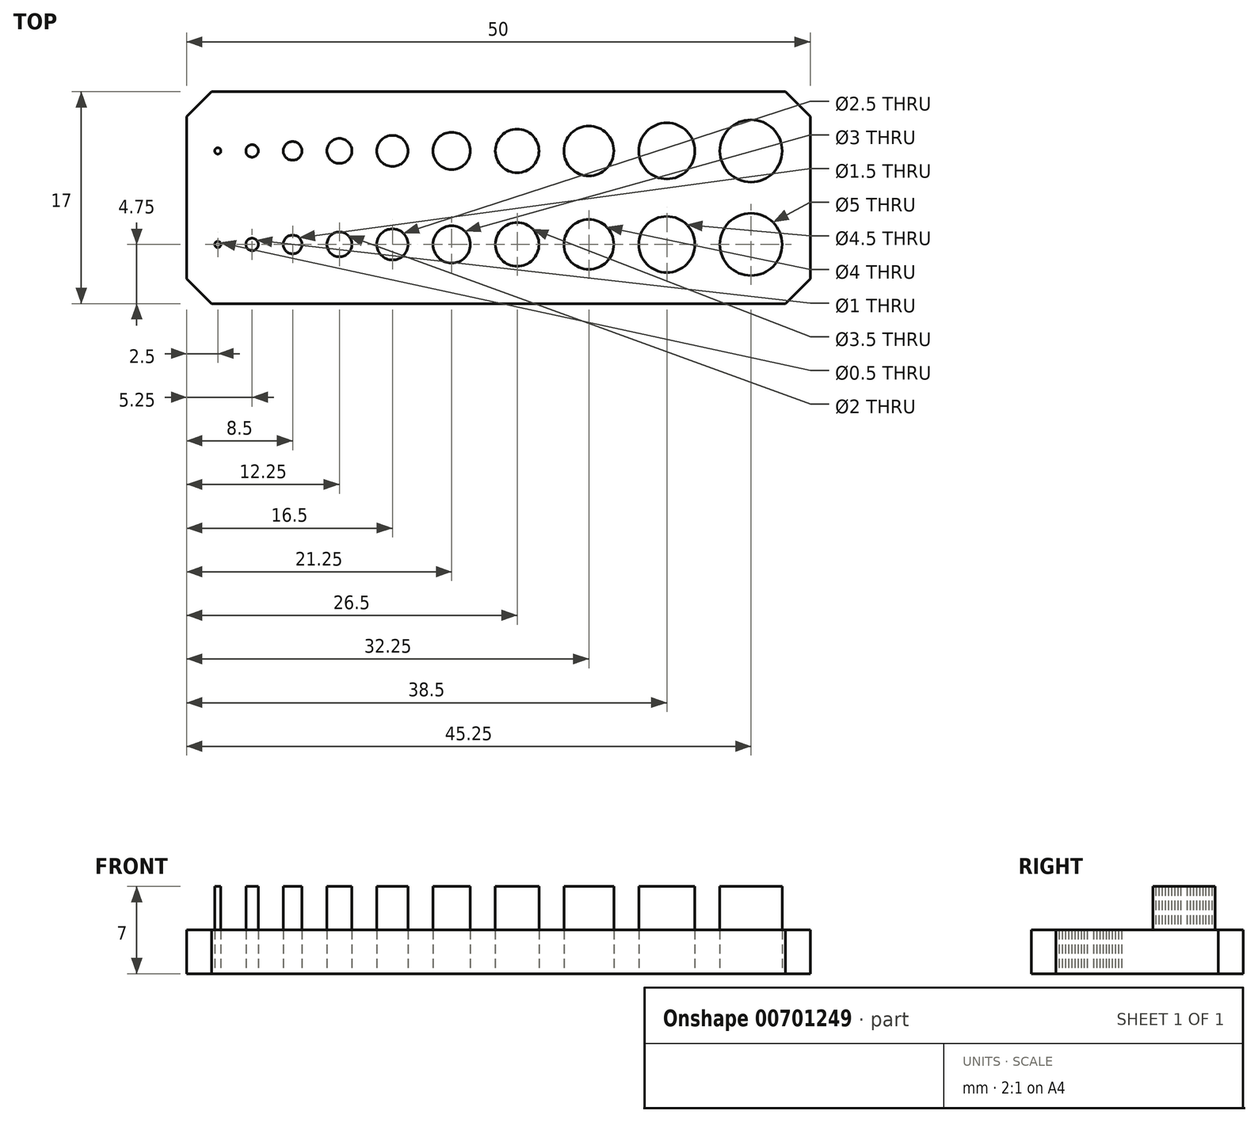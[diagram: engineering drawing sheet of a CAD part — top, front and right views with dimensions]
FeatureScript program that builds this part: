
annotation { "Feature Type Name" : "Feature", "Feature Type Description" : "" }
export const myFeature = defineFeature(function(context is Context, id is Id, definition is map)
    precondition{}
    {
        {
            var Q0;
            Q0=qCreatedBy(makeId("Top.planeOp"),FACE);
            var sketch = newSketch(context, id + "F0", { "sketchPlane" : qUnion([Q0])});
            skLineSegment(sketch, "E0.bottom", {"start": v(25, 8.5) * mm, "end": v(-25, 8.5) * mm});
            skLineSegment(sketch, "E0.top", {"start": v(25, -8.5) * mm, "end": v(-25, -8.5) * mm});
            skLineSegment(sketch, "E0.left", {"start": v(25, 8.5) * mm, "end": v(25, -8.5) * mm});
            skLineSegment(sketch, "E0.right", {"start": v(-25, 8.5) * mm, "end": v(-25, -8.5) * mm});
            skPoint(sketch, "E0.middle", {"position": v(0, 0) * mm});
            skCircle(sketch, "E1", {"center": v(-22.5, 3.75) * mm, "radius": 0.25 * mm});
            skCircle(sketch, "E2", {"center": v(-19.75, 3.75) * mm, "radius": 0.5 * mm});
            skLineSegment(sketch, "E3", {"start": v(-22.25, 3.75) * mm, "end": v(-20.25, 3.75) * mm, "construction": true});
            skLineSegment(sketch, "E4", {"start": v(-19.25, 3.75) * mm, "end": v(-17.25, 3.75) * mm, "construction": true});
            skCircle(sketch, "E5", {"center": v(-16.5, 3.75) * mm, "radius": 0.75 * mm});
            skLineSegment(sketch, "E6", {"start": v(-15.75, 3.75) * mm, "end": v(-13.75, 3.75) * mm, "construction": true});
            skCircle(sketch, "E7", {"center": v(-12.75, 3.75) * mm, "radius": 1 * mm});
            skLineSegment(sketch, "E8", {"start": v(-11.75, 3.75) * mm, "end": v(-9.75, 3.75) * mm, "construction": true});
            skCircle(sketch, "E9", {"center": v(-8.5, 3.75) * mm, "radius": 1.25 * mm});
            skLineSegment(sketch, "E10", {"start": v(-7.25, 3.75) * mm, "end": v(-5.25, 3.75) * mm, "construction": true});
            skCircle(sketch, "E11", {"center": v(-3.75, 3.75) * mm, "radius": 1.5 * mm});
            skLineSegment(sketch, "E12", {"start": v(-2.25, 3.75) * mm, "end": v(-0.25, 3.75) * mm, "construction": true});
            skCircle(sketch, "E13", {"center": v(1.5, 3.75) * mm, "radius": 1.75 * mm});
            skLineSegment(sketch, "E14", {"start": v(3.25, 3.75) * mm, "end": v(5.25, 3.75) * mm, "construction": true});
            skCircle(sketch, "E15", {"center": v(7.25, 3.75) * mm, "radius": 2 * mm});
            skLineSegment(sketch, "E16", {"start": v(9.25, 3.75) * mm, "end": v(11.25, 3.75) * mm, "construction": true});
            skCircle(sketch, "E17", {"center": v(13.5, 3.75) * mm, "radius": 2.25 * mm});
            skLineSegment(sketch, "E18", {"start": v(15.75, 3.75) * mm, "end": v(17.75, 3.75) * mm, "construction": true});
            skCircle(sketch, "E19", {"center": v(20.25, 3.75) * mm, "radius": 2.5 * mm});
            skLineSegment(sketch, "E20", {"start": v(22.75, 3.75) * mm, "end": v(25, 3.75) * mm, "construction": true});
            skLineSegment(sketch, "E21", {"start": v(-22.75, 3.75) * mm, "end": v(-25, 3.75) * mm, "construction": true});
            skLineSegment(sketch, "E22", {"start": v(0, 0) * mm, "end": v(7.3, 0) * mm, "construction": true});
            skCircle(sketch, "E23.MirrorC", {"center": v(-22.5, -3.75) * mm, "radius": 0.25 * mm});
            skCircle(sketch, "E24.MirrorC", {"center": v(1.5, -3.75) * mm, "radius": 1.75 * mm});
            skCircle(sketch, "E25.MirrorC", {"center": v(-19.75, -3.75) * mm, "radius": 0.5 * mm});
            skCircle(sketch, "E26.MirrorC", {"center": v(7.25, -3.75) * mm, "radius": 2 * mm});
            skCircle(sketch, "E27.MirrorC", {"center": v(13.5, -3.75) * mm, "radius": 2.25 * mm});
            skCircle(sketch, "E28.MirrorC", {"center": v(20.25, -3.75) * mm, "radius": 2.5 * mm});
            skCircle(sketch, "E29.MirrorC", {"center": v(-16.5, -3.75) * mm, "radius": 0.75 * mm});
            skCircle(sketch, "E30.MirrorC", {"center": v(-3.75, -3.75) * mm, "radius": 1.5 * mm});
            skCircle(sketch, "E31.MirrorC", {"center": v(-8.5, -3.75) * mm, "radius": 1.25 * mm});
            skCircle(sketch, "E32.MirrorC", {"center": v(-12.75, -3.75) * mm, "radius": 1 * mm});
            skLineSegment(sketch, "E33", {"start": v(20.25, 6.25) * mm, "end": v(20.25, 8.5) * mm, "construction": true});
            skSolve(sketch);
        }
        {
            var Q0;
            Q0=qSketchRegion(id+"F0",true);
            extrude(context, id + "F1", {"entities" : qUnion([Q0]), "depth" : 3.5 * mm, "offsetDistance" : 25 * mm});
        }
        {
            var Q0;
            Q0=makeQuery(id+"F0.imprint","IMPRINT",FACE,{"disambiguationData":[TD([[makeQuery(id+"F0.imprint","IMPRINT",EDGE,{"derivedFrom":sQuery(id+"F0.wireOp",EDGE,"E1")}),1.0]])]});
            var Q1;
            Q1=makeQuery(id+"F0.imprint","IMPRINT",FACE,{"disambiguationData":[TD([[makeQuery(id+"F0.imprint","IMPRINT",EDGE,{"derivedFrom":sQuery(id+"F0.wireOp",EDGE,"E2")}),1.0]])]});
            var Q2;
            Q2=makeQuery(id+"F0.imprint","IMPRINT",FACE,{"disambiguationData":[TD([[makeQuery(id+"F0.imprint","IMPRINT",EDGE,{"derivedFrom":sQuery(id+"F0.wireOp",EDGE,"E5")}),1.0]])]});
            var Q3;
            Q3=makeQuery(id+"F0.imprint","IMPRINT",FACE,{"disambiguationData":[TD([[makeQuery(id+"F0.imprint","IMPRINT",EDGE,{"derivedFrom":sQuery(id+"F0.wireOp",EDGE,"E7")}),1.0]])]});
            var Q4;
            Q4=makeQuery(id+"F0.imprint","IMPRINT",FACE,{"disambiguationData":[TD([[makeQuery(id+"F0.imprint","IMPRINT",EDGE,{"derivedFrom":sQuery(id+"F0.wireOp",EDGE,"E9")}),1.0]])]});
            var Q5;
            Q5=makeQuery(id+"F0.imprint","IMPRINT",FACE,{"disambiguationData":[TD([[makeQuery(id+"F0.imprint","IMPRINT",EDGE,{"derivedFrom":sQuery(id+"F0.wireOp",EDGE,"E11")}),1.0]])]});
            var Q6;
            Q6=makeQuery(id+"F0.imprint","IMPRINT",FACE,{"disambiguationData":[TD([[makeQuery(id+"F0.imprint","IMPRINT",EDGE,{"derivedFrom":sQuery(id+"F0.wireOp",EDGE,"E13")}),1.0]])]});
            var Q7;
            Q7=makeQuery(id+"F0.imprint","IMPRINT",FACE,{"disambiguationData":[TD([[makeQuery(id+"F0.imprint","IMPRINT",EDGE,{"derivedFrom":sQuery(id+"F0.wireOp",EDGE,"E15")}),1.0]])]});
            var Q8;
            Q8=makeQuery(id+"F0.imprint","IMPRINT",FACE,{"disambiguationData":[TD([[makeQuery(id+"F0.imprint","IMPRINT",EDGE,{"derivedFrom":sQuery(id+"F0.wireOp",EDGE,"E17")}),1.0]])]});
            var Q9;
            Q9=makeQuery(id+"F0.imprint","IMPRINT",FACE,{"disambiguationData":[TD([[makeQuery(id+"F0.imprint","IMPRINT",EDGE,{"derivedFrom":sQuery(id+"F0.wireOp",EDGE,"E19")}),1.0]])]});
            var Q10;
            Q10=makeQuery(id+"F1.opExtrude","CAP_FACE",FACE,{"disambiguationData":[OSD([sQuery(id+"F0.wireOp",EDGE,"E0.bottom"),sQuery(id+"F0.wireOp",EDGE,"E0.top"),sQuery(id+"F0.wireOp",EDGE,"E0.left"),sQuery(id+"F0.wireOp",EDGE,"E0.right"),sQuery(id+"F0.wireOp",EDGE,"E1"),sQuery(id+"F0.wireOp",EDGE,"E2"),sQuery(id+"F0.wireOp",EDGE,"E5"),sQuery(id+"F0.wireOp",EDGE,"E7"),sQuery(id+"F0.wireOp",EDGE,"E9"),sQuery(id+"F0.wireOp",EDGE,"E11"),sQuery(id+"F0.wireOp",EDGE,"E13"),sQuery(id+"F0.wireOp",EDGE,"E15"),sQuery(id+"F0.wireOp",EDGE,"E17"),sQuery(id+"F0.wireOp",EDGE,"E19"),sQuery(id+"F0.wireOp",EDGE,"E23.MirrorC"),sQuery(id+"F0.wireOp",EDGE,"E24.MirrorC"),sQuery(id+"F0.wireOp",EDGE,"E25.MirrorC"),sQuery(id+"F0.wireOp",EDGE,"E26.MirrorC"),sQuery(id+"F0.wireOp",EDGE,"E27.MirrorC"),sQuery(id+"F0.wireOp",EDGE,"E28.MirrorC"),sQuery(id+"F0.wireOp",EDGE,"E29.MirrorC"),sQuery(id+"F0.wireOp",EDGE,"E30.MirrorC"),sQuery(id+"F0.wireOp",EDGE,"E31.MirrorC"),sQuery(id+"F0.wireOp",EDGE,"E32.MirrorC")])],"isStart":false});
            extrude(context, id + "F2", {"entities" : qUnion([Q0, Q1, Q2, Q3, Q4, Q5, Q6, Q7, Q8, Q9]), "operationType" : NewBodyOperationType.ADD, "endBound" : BoundingType.UP_TO_SURFACE, "depth" : 25 * mm, "endBoundEntityFace" : qUnion([Q10]), "hasOffset" : true, "offsetDistance" : 3.5 * mm, "offsetOppositeDirection" : true});
        }
        {
            var Q0;
            Q0=makeQuery(id+"F1.opExtrude","SWEPT_EDGE",EDGE,{"disambiguationData":[OSD([sQuery(id+"F0.wireOp",EDGE,"E0.top"),sQuery(id+"F0.wireOp",EDGE,"E0.right")])]});
            var Q1;
            Q1=makeQuery(id+"F1.opExtrude","SWEPT_EDGE",EDGE,{"disambiguationData":[OSD([sQuery(id+"F0.wireOp",EDGE,"E0.bottom"),sQuery(id+"F0.wireOp",EDGE,"E0.right")])]});
            var Q2;
            Q2=makeQuery(id+"F1.opExtrude","SWEPT_EDGE",EDGE,{"disambiguationData":[OSD([sQuery(id+"F0.wireOp",EDGE,"E0.top"),sQuery(id+"F0.wireOp",EDGE,"E0.left")])]});
            var Q3;
            Q3=makeQuery(id+"F1.opExtrude","SWEPT_EDGE",EDGE,{"disambiguationData":[OSD([sQuery(id+"F0.wireOp",EDGE,"E0.bottom"),sQuery(id+"F0.wireOp",EDGE,"E0.left")])]});
            chamfer(context, id + "F3", {"entities" : qUnion([Q0, Q1, Q2, Q3]), "width" : 2 * mm, "tangentPropagation" : true});
        }
    });
